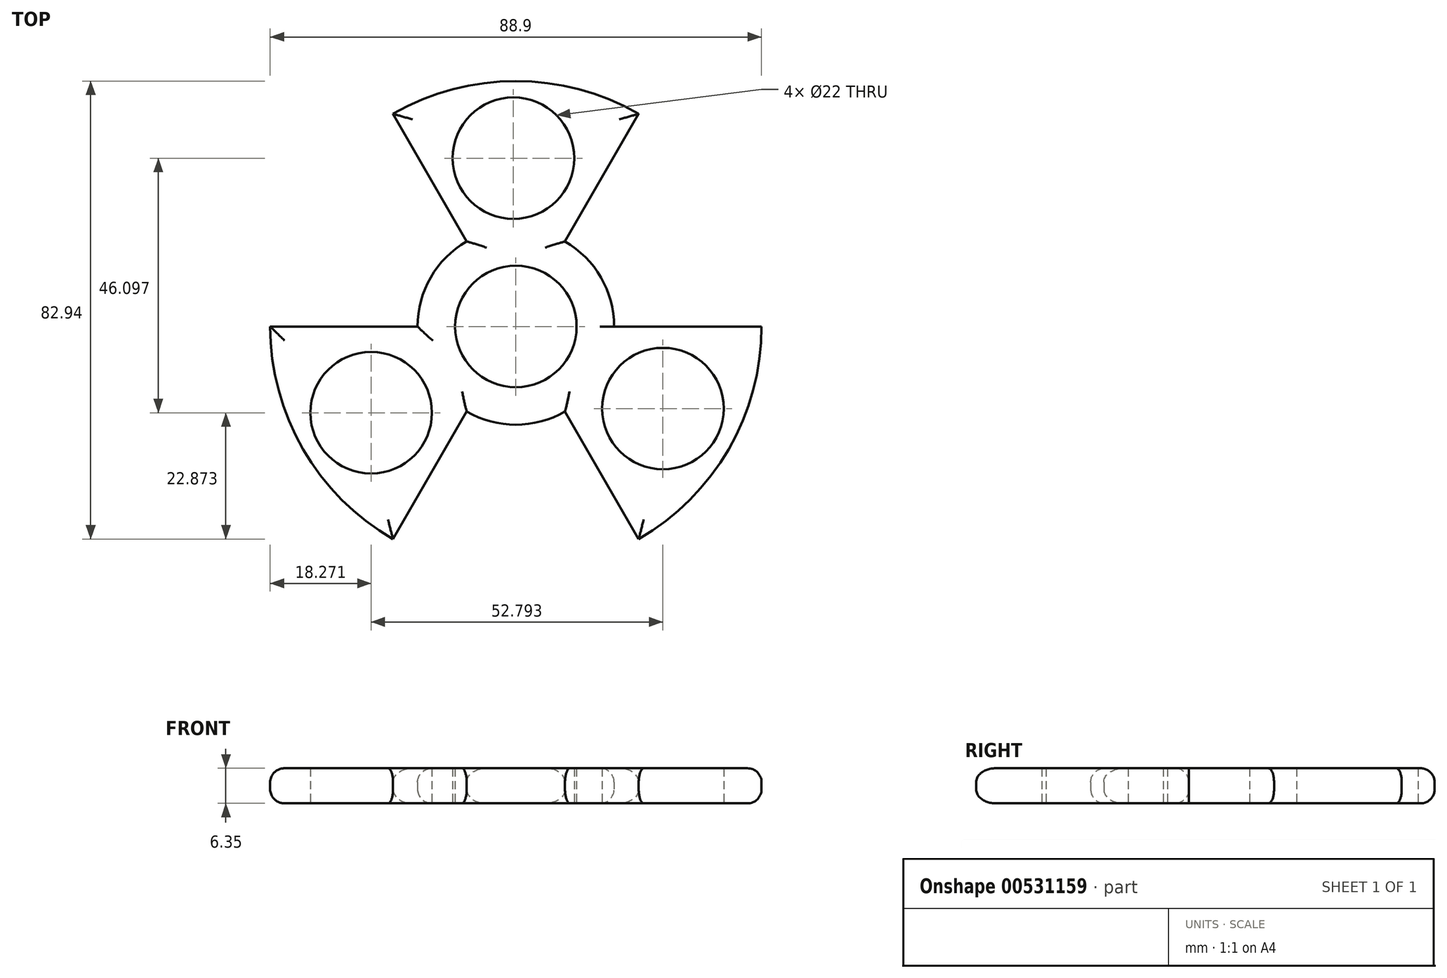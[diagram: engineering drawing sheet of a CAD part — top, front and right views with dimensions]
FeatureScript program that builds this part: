
annotation { "Feature Type Name" : "Feature", "Feature Type Description" : "" }
export const myFeature = defineFeature(function(context is Context, id is Id, definition is map)
    precondition{}
    {
        {
            var Q0;
            Q0=qCreatedBy(makeId("Top.planeOp"),FACE);
            var sketch = newSketch(context, id + "F0", { "sketchPlane" : qUnion([Q0])});
            skCircle(sketch, "E0", {"center": v(0, 0) * mm, "radius": 44.45 * mm});
            skCircle(sketch, "E1", {"center": v(0, 0) * mm, "radius": 11 * mm});
            skCircle(sketch, "E2", {"center": v(-0.43, 30.48) * mm, "radius": 11 * mm});
            skCircle(sketch, "E3.1.0", {"center": v(-26.18, -15.62) * mm, "radius": 11 * mm});
            skCircle(sketch, "E3.2.0", {"center": v(26.61, -14.86) * mm, "radius": 11 * mm});
            skPoint(sketch, "E4.orphan", {"position": v(44.45, 0) * mm});
            skLineSegment(sketch, "E5", {"start": v(44.45, 0) * mm, "end": v(13.97, 0) * mm});
            skPoint(sketch, "E6.start.orphan", {"position": v(-44.45, 0) * mm});
            skCircle(sketch, "E7", {"center": v(0, 0) * mm, "radius": 17.78 * mm});
            skLineSegment(sketch, "E8", {"start": v(44.45, 0) * mm, "end": v(17.78, 0) * mm});
            skLineSegment(sketch, "E9", {"start": v(-17.78, 0) * mm, "end": v(-44.45, 0) * mm});
            skLineSegment(sketch, "E10.1.0", {"start": v(-22.23, 38.5) * mm, "end": v(-8.89, 15.4) * mm});
            skLineSegment(sketch, "E10.1.1", {"start": v(8.89, -15.4) * mm, "end": v(22.23, -38.5) * mm});
            skLineSegment(sketch, "E10.2.0", {"start": v(-22.23, -38.5) * mm, "end": v(-8.9, -15.4) * mm});
            skLineSegment(sketch, "E10.2.1", {"start": v(8.9, 15.4) * mm, "end": v(22.23, 38.5) * mm});
            skSolve(sketch);
        }
        {
            var Q0;
            Q0=makeQuery(id+"F0.imprint","IMPRINT",FACE,{"disambiguationData":[TD([[makeQuery(id+"F0.imprint","IMPRINT",EDGE,{"derivedFrom":sQuery(id+"F0.wireOp",EDGE,"E3.1.0")}),-1.0]])]});
            var Q1;
            Q1=makeQuery(id+"F0.imprint","IMPRINT",FACE,{"disambiguationData":[TD([[makeQuery(id+"F0.imprint","IMPRINT",EDGE,{"derivedFrom":sQuery(id+"F0.wireOp",EDGE,"E2")}),-1.0]])]});
            var Q2;
            Q2=makeQuery(id+"F0.imprint","IMPRINT",FACE,{"disambiguationData":[TD([[makeQuery(id+"F0.imprint","IMPRINT",EDGE,{"derivedFrom":sQuery(id+"F0.wireOp",EDGE,"E3.2.0")}),-1.0]])]});
            var Q3;
            Q3=makeQuery(id+"F0.imprint","IMPRINT",FACE,{"disambiguationData":[TD([[makeQuery(id+"F0.imprint","IMPRINT",EDGE,{"derivedFrom":sQuery(id+"F0.wireOp",EDGE,"E1")}),-1.0]])]});
            extrude(context, id + "F1", {"entities" : qUnion([Q0, Q1, Q2, Q3]), "depth" : 6.35 * mm, "offsetDistance" : 25.4 * mm});
        }
        {
            var Q0;
            {var subQ0=sQuery(id+"F0.wireOp",EDGE,"E0");Q0=makeQuery(id+"F1.opExtrude","CAP_EDGE",EDGE,{"disambiguationData":[OSD([subQ0]),TDD([makeQuery(id+"F0.imprint","IMPRINT",EDGE,{"disambiguationData":[TD([[makeQuery(id+"F0.imprint","INTERSECT",VERTEX,{"derivedFrom":[subQ0,sQuery(id+"F0.wireOp",EDGE,"E9")]}),-1.0]])],"derivedFrom":subQ0})])],"isStart":false});}
            var Q1;
            Q1=makeQuery(id+"F1.opExtrude","CAP_EDGE",EDGE,{"disambiguationData":[OSD([sQuery(id+"F0.wireOp",EDGE,"E10.2.0")])],"isStart":false});
            var Q2;
            {var subQ0=sQuery(id+"F0.wireOp",EDGE,"E7");Q2=makeQuery(id+"F1.opExtrude","CAP_EDGE",EDGE,{"disambiguationData":[OSD([subQ0]),TDD([makeQuery(id+"F0.imprint","IMPRINT",EDGE,{"disambiguationData":[TD([[makeQuery(id+"F0.imprint","INTERSECT",VERTEX,{"derivedFrom":[subQ0,sQuery(id+"F0.wireOp",EDGE,"E10.1.1")]}),1.0]])],"derivedFrom":subQ0})])],"isStart":false});}
            var Q3;
            Q3=makeQuery(id+"F1.opExtrude","CAP_EDGE",EDGE,{"disambiguationData":[OSD([sQuery(id+"F0.wireOp",EDGE,"E10.1.1")])],"isStart":false});
            var Q4;
            {var subQ0=sQuery(id+"F0.wireOp",EDGE,"E0");Q4=makeQuery(id+"F1.opExtrude","CAP_EDGE",EDGE,{"disambiguationData":[OSD([subQ0]),TDD([makeQuery(id+"F0.imprint","IMPRINT",EDGE,{"disambiguationData":[TD([[makeQuery(id+"F0.imprint","INTERSECT",VERTEX,{"derivedFrom":[subQ0,sQuery(id+"F0.wireOp",EDGE,"E8")]}),1.0]])],"derivedFrom":subQ0})])],"isStart":false});}
            var Q5;
            Q5=makeQuery(id+"F1.opExtrude","CAP_EDGE",EDGE,{"disambiguationData":[OSD([sQuery(id+"F0.wireOp",EDGE,"E8")])],"isStart":false});
            var Q6;
            {var subQ0=sQuery(id+"F0.wireOp",EDGE,"E7");Q6=makeQuery(id+"F1.opExtrude","CAP_EDGE",EDGE,{"disambiguationData":[OSD([subQ0]),TDD([makeQuery(id+"F0.imprint","IMPRINT",EDGE,{"disambiguationData":[TD([[makeQuery(id+"F0.imprint","INTERSECT",VERTEX,{"derivedFrom":[subQ0,sQuery(id+"F0.wireOp",EDGE,"E8")]}),-1.0]])],"derivedFrom":subQ0})])],"isStart":false});}
            var Q7;
            Q7=makeQuery(id+"F1.opExtrude","CAP_EDGE",EDGE,{"disambiguationData":[OSD([sQuery(id+"F0.wireOp",EDGE,"E10.2.1")])],"isStart":false});
            var Q8;
            {var subQ0=sQuery(id+"F0.wireOp",EDGE,"E0");Q8=makeQuery(id+"F1.opExtrude","CAP_EDGE",EDGE,{"disambiguationData":[OSD([subQ0]),TDD([makeQuery(id+"F0.imprint","IMPRINT",EDGE,{"disambiguationData":[TD([[makeQuery(id+"F0.imprint","INTERSECT",VERTEX,{"derivedFrom":[subQ0,sQuery(id+"F0.wireOp",EDGE,"E10.1.0")]}),1.0]])],"derivedFrom":subQ0})])],"isStart":false});}
            var Q9;
            Q9=makeQuery(id+"F1.opExtrude","CAP_EDGE",EDGE,{"disambiguationData":[OSD([sQuery(id+"F0.wireOp",EDGE,"E10.1.0")])],"isStart":false});
            var Q10;
            {var subQ0=sQuery(id+"F0.wireOp",EDGE,"E7");Q10=makeQuery(id+"F1.opExtrude","CAP_EDGE",EDGE,{"disambiguationData":[OSD([subQ0]),TDD([makeQuery(id+"F0.imprint","IMPRINT",EDGE,{"disambiguationData":[TD([[makeQuery(id+"F0.imprint","INTERSECT",VERTEX,{"derivedFrom":[subQ0,sQuery(id+"F0.wireOp",EDGE,"E9")]}),1.0]])],"derivedFrom":subQ0})])],"isStart":false});}
            var Q11;
            Q11=makeQuery(id+"F1.opExtrude","CAP_EDGE",EDGE,{"disambiguationData":[OSD([sQuery(id+"F0.wireOp",EDGE,"E9")])],"isStart":false});
            var Q12;
            Q12=makeQuery(id+"F1.opExtrude","CAP_EDGE",EDGE,{"disambiguationData":[OSD([sQuery(id+"F0.wireOp",EDGE,"E10.1.0")])],"isStart":true});
            var Q13;
            {var subQ0=sQuery(id+"F0.wireOp",EDGE,"E0");Q13=makeQuery(id+"F1.opExtrude","CAP_EDGE",EDGE,{"disambiguationData":[OSD([subQ0]),TDD([makeQuery(id+"F0.imprint","IMPRINT",EDGE,{"disambiguationData":[TD([[makeQuery(id+"F0.imprint","INTERSECT",VERTEX,{"derivedFrom":[subQ0,sQuery(id+"F0.wireOp",EDGE,"E10.1.0")]}),1.0]])],"derivedFrom":subQ0})])],"isStart":true});}
            var Q14;
            Q14=makeQuery(id+"F1.opExtrude","CAP_EDGE",EDGE,{"disambiguationData":[OSD([sQuery(id+"F0.wireOp",EDGE,"E10.2.1")])],"isStart":true});
            var Q15;
            {var subQ0=sQuery(id+"F0.wireOp",EDGE,"E0");Q15=makeQuery(id+"F1.opExtrude","CAP_EDGE",EDGE,{"disambiguationData":[OSD([subQ0]),TDD([makeQuery(id+"F0.imprint","IMPRINT",EDGE,{"disambiguationData":[TD([[makeQuery(id+"F0.imprint","INTERSECT",VERTEX,{"derivedFrom":[subQ0,sQuery(id+"F0.wireOp",EDGE,"E8")]}),1.0]])],"derivedFrom":subQ0})])],"isStart":true});}
            var Q16;
            Q16=makeQuery(id+"F1.opExtrude","CAP_EDGE",EDGE,{"disambiguationData":[OSD([sQuery(id+"F0.wireOp",EDGE,"E8")])],"isStart":true});
            var Q17;
            Q17=makeQuery(id+"F1.opExtrude","CAP_EDGE",EDGE,{"disambiguationData":[OSD([sQuery(id+"F0.wireOp",EDGE,"E10.1.1")])],"isStart":true});
            var Q18;
            {var subQ0=sQuery(id+"F0.wireOp",EDGE,"E7");Q18=makeQuery(id+"F1.opExtrude","CAP_EDGE",EDGE,{"disambiguationData":[OSD([subQ0]),TDD([makeQuery(id+"F0.imprint","IMPRINT",EDGE,{"disambiguationData":[TD([[makeQuery(id+"F0.imprint","INTERSECT",VERTEX,{"derivedFrom":[subQ0,sQuery(id+"F0.wireOp",EDGE,"E9")]}),1.0]])],"derivedFrom":subQ0})])],"isStart":true});}
            var Q19;
            {var subQ0=sQuery(id+"F0.wireOp",EDGE,"E7");Q19=makeQuery(id+"F1.opExtrude","CAP_EDGE",EDGE,{"disambiguationData":[OSD([subQ0]),TDD([makeQuery(id+"F0.imprint","IMPRINT",EDGE,{"disambiguationData":[TD([[makeQuery(id+"F0.imprint","INTERSECT",VERTEX,{"derivedFrom":[subQ0,sQuery(id+"F0.wireOp",EDGE,"E8")]}),-1.0]])],"derivedFrom":subQ0})])],"isStart":true});}
            var Q20;
            Q20=makeQuery(id+"F1.opExtrude","CAP_EDGE",EDGE,{"disambiguationData":[OSD([sQuery(id+"F0.wireOp",EDGE,"E9")])],"isStart":true});
            var Q21;
            {var subQ0=sQuery(id+"F0.wireOp",EDGE,"E0");Q21=makeQuery(id+"F1.opExtrude","CAP_EDGE",EDGE,{"disambiguationData":[OSD([subQ0]),TDD([makeQuery(id+"F0.imprint","IMPRINT",EDGE,{"disambiguationData":[TD([[makeQuery(id+"F0.imprint","INTERSECT",VERTEX,{"derivedFrom":[subQ0,sQuery(id+"F0.wireOp",EDGE,"E9")]}),-1.0]])],"derivedFrom":subQ0})])],"isStart":true});}
            var Q22;
            Q22=makeQuery(id+"F1.opExtrude","CAP_EDGE",EDGE,{"disambiguationData":[OSD([sQuery(id+"F0.wireOp",EDGE,"E10.2.0")])],"isStart":true});
            var Q23;
            {var subQ0=sQuery(id+"F0.wireOp",EDGE,"E7");Q23=makeQuery(id+"F1.opExtrude","CAP_EDGE",EDGE,{"disambiguationData":[OSD([subQ0]),TDD([makeQuery(id+"F0.imprint","IMPRINT",EDGE,{"disambiguationData":[TD([[makeQuery(id+"F0.imprint","INTERSECT",VERTEX,{"derivedFrom":[subQ0,sQuery(id+"F0.wireOp",EDGE,"E10.1.1")]}),1.0]])],"derivedFrom":subQ0})])],"isStart":true});}
            fillet(context, id + "F2", {"entities" : qUnion([Q0, Q1, Q2, Q3, Q4, Q5, Q6, Q7, Q8, Q9, Q10, Q11, Q12, Q13, Q14, Q15, Q16, Q17, Q18, Q19, Q20, Q21, Q22, Q23]), "radius" : 2.54 * mm, "tangentPropagation" : true, "allowEdgeOverflow" : false});
        }
    });
